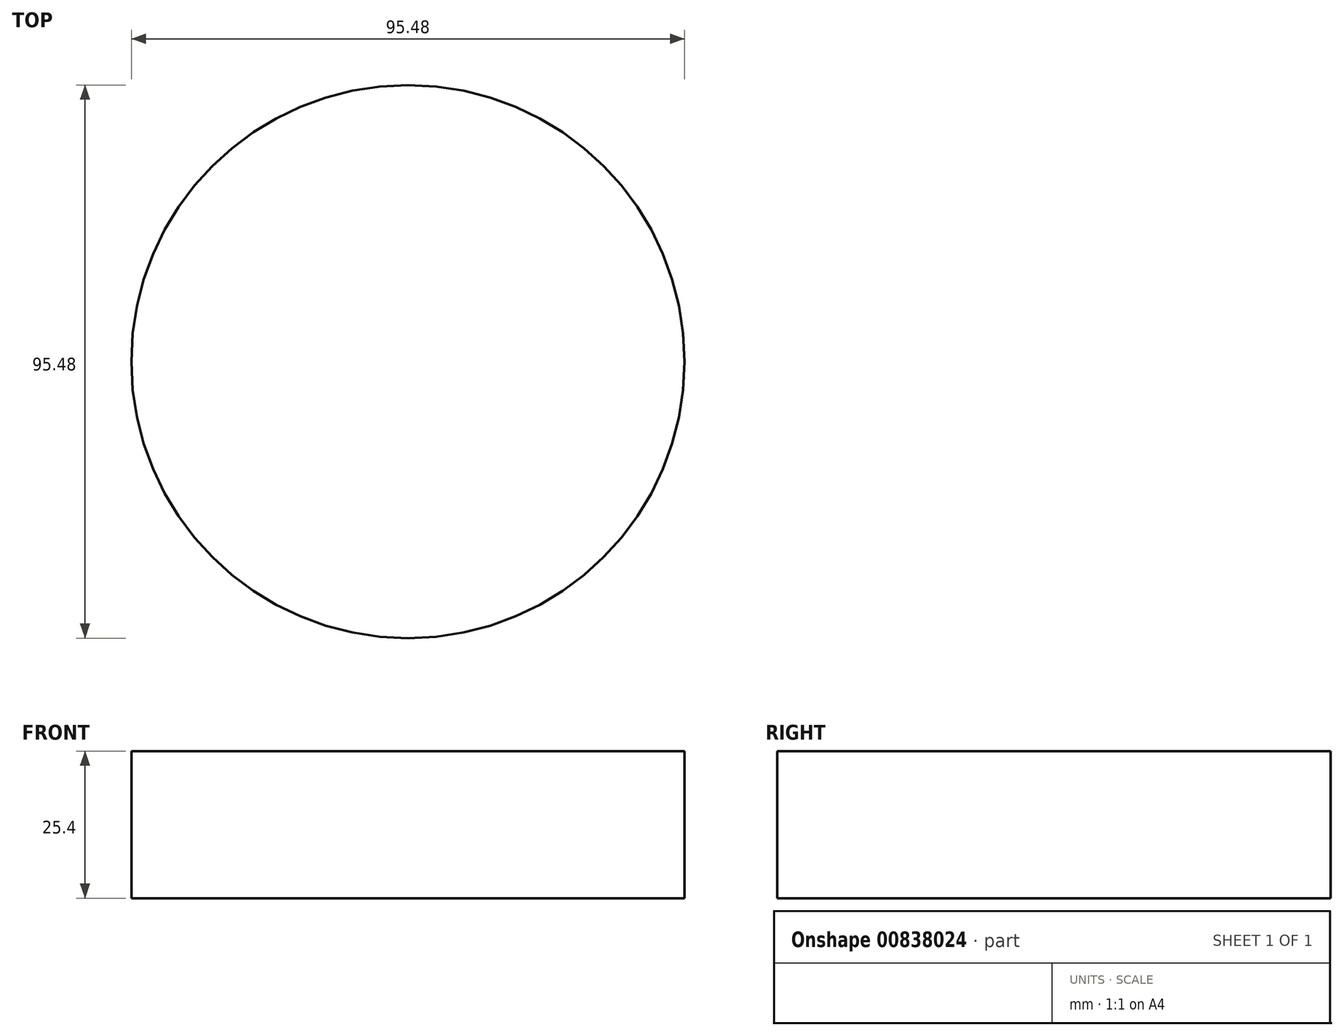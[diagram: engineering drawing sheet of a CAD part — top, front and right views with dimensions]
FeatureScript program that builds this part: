
annotation { "Feature Type Name" : "Feature", "Feature Type Description" : "" }
export const myFeature = defineFeature(function(context is Context, id is Id, definition is map)
    precondition{}
    {
        {
            var Q0;
            Q0=qCreatedBy(makeId("Top.planeOp"),FACE);
            var sketch = newSketch(context, id + "F0", { "sketchPlane" : qUnion([Q0])});
            skCircle(sketch, "E0", {"center": v(0, 0) * mm, "radius": 47.74 * mm});
            skSolve(sketch);
        }
        {
            var Q0;
            Q0=makeQuery(id+"F0.imprint","IMPRINT",FACE,{"disambiguationData":[TD([[makeQuery(id+"F0.imprint","IMPRINT",EDGE,{"derivedFrom":sQuery(id+"F0.wireOp",EDGE,"E0")}),1.0]])]});
            extrude(context, id + "F1", {"entities" : qUnion([Q0]), "depth" : 25.4 * mm, "offsetDistance" : 25.4 * mm});
        }
    });
